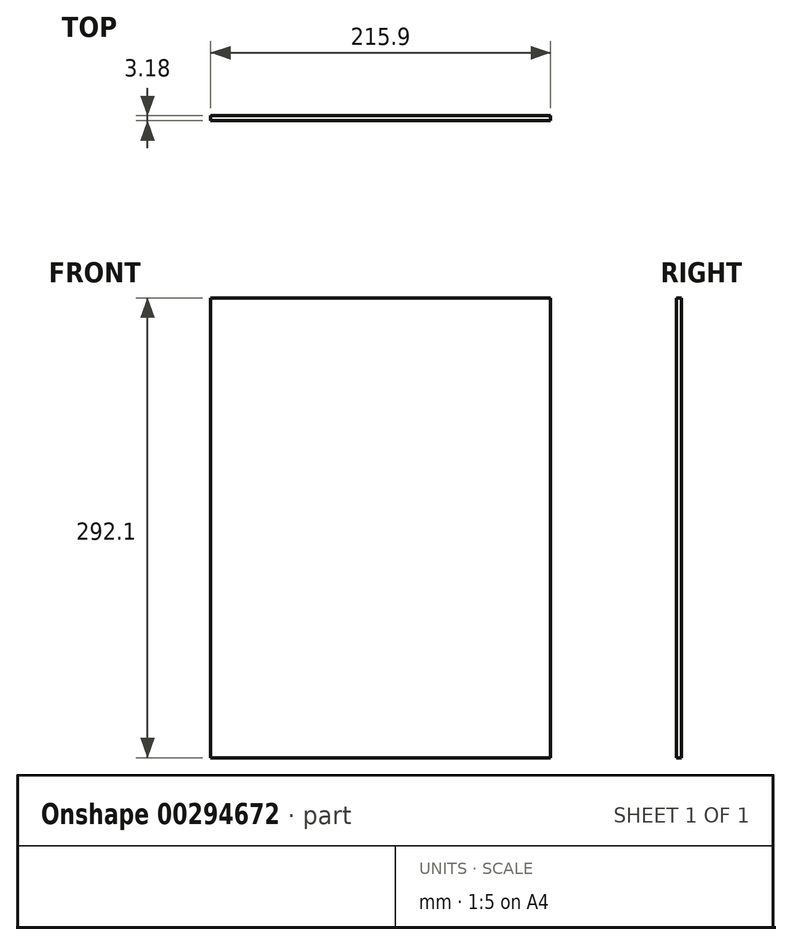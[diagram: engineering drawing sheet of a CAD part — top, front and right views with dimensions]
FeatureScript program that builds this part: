
annotation { "Feature Type Name" : "Feature", "Feature Type Description" : "" }
export const myFeature = defineFeature(function(context is Context, id is Id, definition is map)
    precondition{}
    {
        {
            var Q0;
            Q0=qCreatedBy(makeId("Front.planeOp"),FACE);
            var sketch = newSketch(context, id + "F0", { "sketchPlane" : qUnion([Q0])});
            skLineSegment(sketch, "E0.bottom", {"start": v(-108.68, 140.27) * mm, "end": v(107.22, 140.27) * mm});
            skLineSegment(sketch, "E0.top", {"start": v(-108.68, -151.83) * mm, "end": v(107.22, -151.83) * mm});
            skLineSegment(sketch, "E0.left", {"start": v(-108.68, 140.27) * mm, "end": v(-108.68, -151.83) * mm});
            skLineSegment(sketch, "E0.right", {"start": v(107.22, 140.27) * mm, "end": v(107.22, -151.83) * mm});
            skSolve(sketch);
        }
        {
            var Q0;
            Q0=makeQuery(id+"F0.imprint","IMPRINT",FACE,{"disambiguationData":[TD([[makeQuery(id+"F0.imprint","IMPRINT",EDGE,{"derivedFrom":sQuery(id+"F0.wireOp",EDGE,"E0.bottom")}),-1.0]])]});
            extrude(context, id + "F1", {"entities" : qUnion([Q0]), "endBound" : BoundingType.SYMMETRIC, "depth" : 3.17 * mm});
        }
    });
